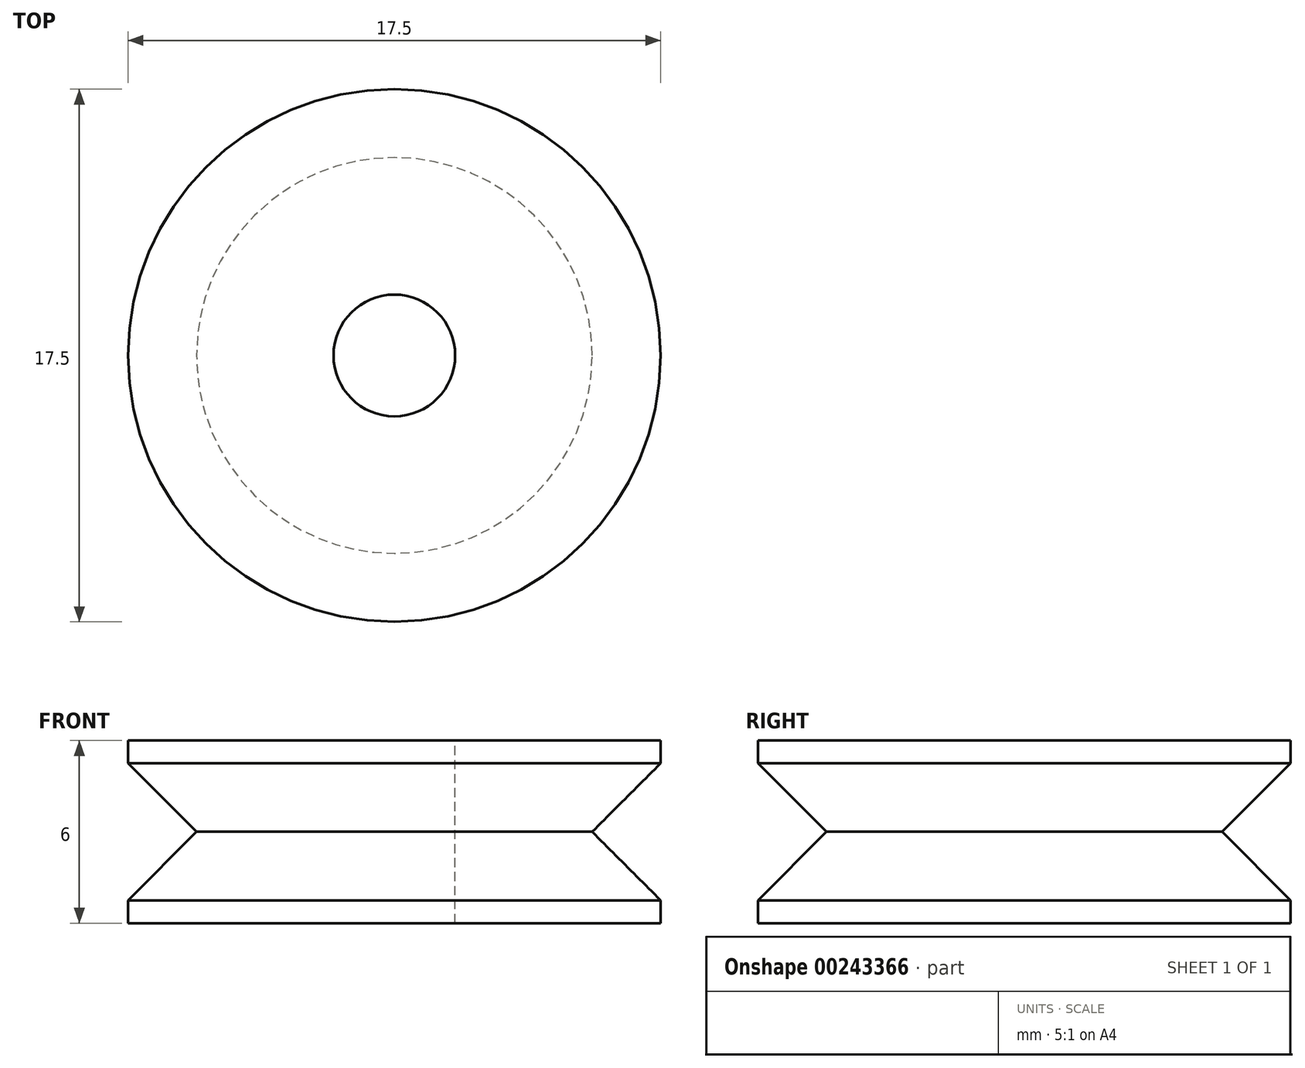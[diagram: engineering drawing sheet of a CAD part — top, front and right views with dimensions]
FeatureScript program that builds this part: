
annotation { "Feature Type Name" : "Feature", "Feature Type Description" : "" }
export const myFeature = defineFeature(function(context is Context, id is Id, definition is map)
    precondition{}
    {
        {
            var Q0;
            Q0=qCreatedBy(makeId("Top.planeOp"),FACE);
            var sketch = newSketch(context, id + "F0", { "sketchPlane" : qUnion([Q0])});
            skCircle(sketch, "E0", {"center": v(0, 0) * mm, "radius": 6.5 * mm});
            skSolve(sketch);
        }
        {
            var Q0;
            Q0 = qSketchRegion(id + "F0", true);
            extrude(context, id + "F1", {"entities" : qUnion([Q0]), "depth" : 2.25 * mm, "hasDraft" : true, "draftAngle" : 45 * degree});
        }
        {
            var Q0;
            Q0=makeQuery(id+"F1.opExtrude","CAP_FACE",FACE,{"disambiguationData":[OSD([sQuery(id+"F0.wireOp",EDGE,"E0")])],"isStart":false});
            extrude(context, id + "F2", {"entities" : qUnion([Q0]), "operationType" : NewBodyOperationType.ADD, "depth" : .75 * mm});
        }
        {
            var Q0;
            Q0=makeQuery(id+"F1.opExtrude","SWEPT_BODY",BODY,{"disambiguationData":[OSD([sQuery(id+"F0.wireOp",EDGE,"E0")])]});
            var Q1;
            Q1=qCreatedBy(makeId("Top.planeOp"),FACE);
            mirror(context, id + "F3", {"operationType" : NewBodyOperationType.ADD, "entities" : qUnion([Q0]), "mirrorPlane" : qUnion([Q1])});
        }
        {
            var Q0;
            Q0=makeQuery(id+"F2.opExtrude","CAP_FACE",FACE,{"disambiguationData":[OSD([sQuery(id+"F0.wireOp",EDGE,"E0")])],"isStart":false});
            var sketch = newSketch(context, id + "F4", { "sketchPlane" : qUnion([Q0])});
            skCircle(sketch, "E1", {"center": v(0, 0) * mm, "radius": 2 * mm});
            skSolve(sketch);
        }
        {
            var Q0;
            Q0 = qSketchRegion(id + "F4", true);
            var Q1;
            Q1=makeQuery(id+"F3.opPattern","COPY",FACE,{"derivedFrom":makeQuery(id+"F2.opExtrude","CAP_FACE",FACE,{"disambiguationData":[OSD([sQuery(id+"F0.wireOp",EDGE,"E0")])],"isStart":false}),"instanceName":"1"});
            extrude(context, id + "F5", {"entities" : qUnion([Q0]), "operationType" : NewBodyOperationType.REMOVE, "endBound" : BoundingType.UP_TO_SURFACE, "oppositeDirection" : true, "endBoundEntityFace" : qUnion([Q1]), "depth" : 25.4 * mm});
        }
    });
